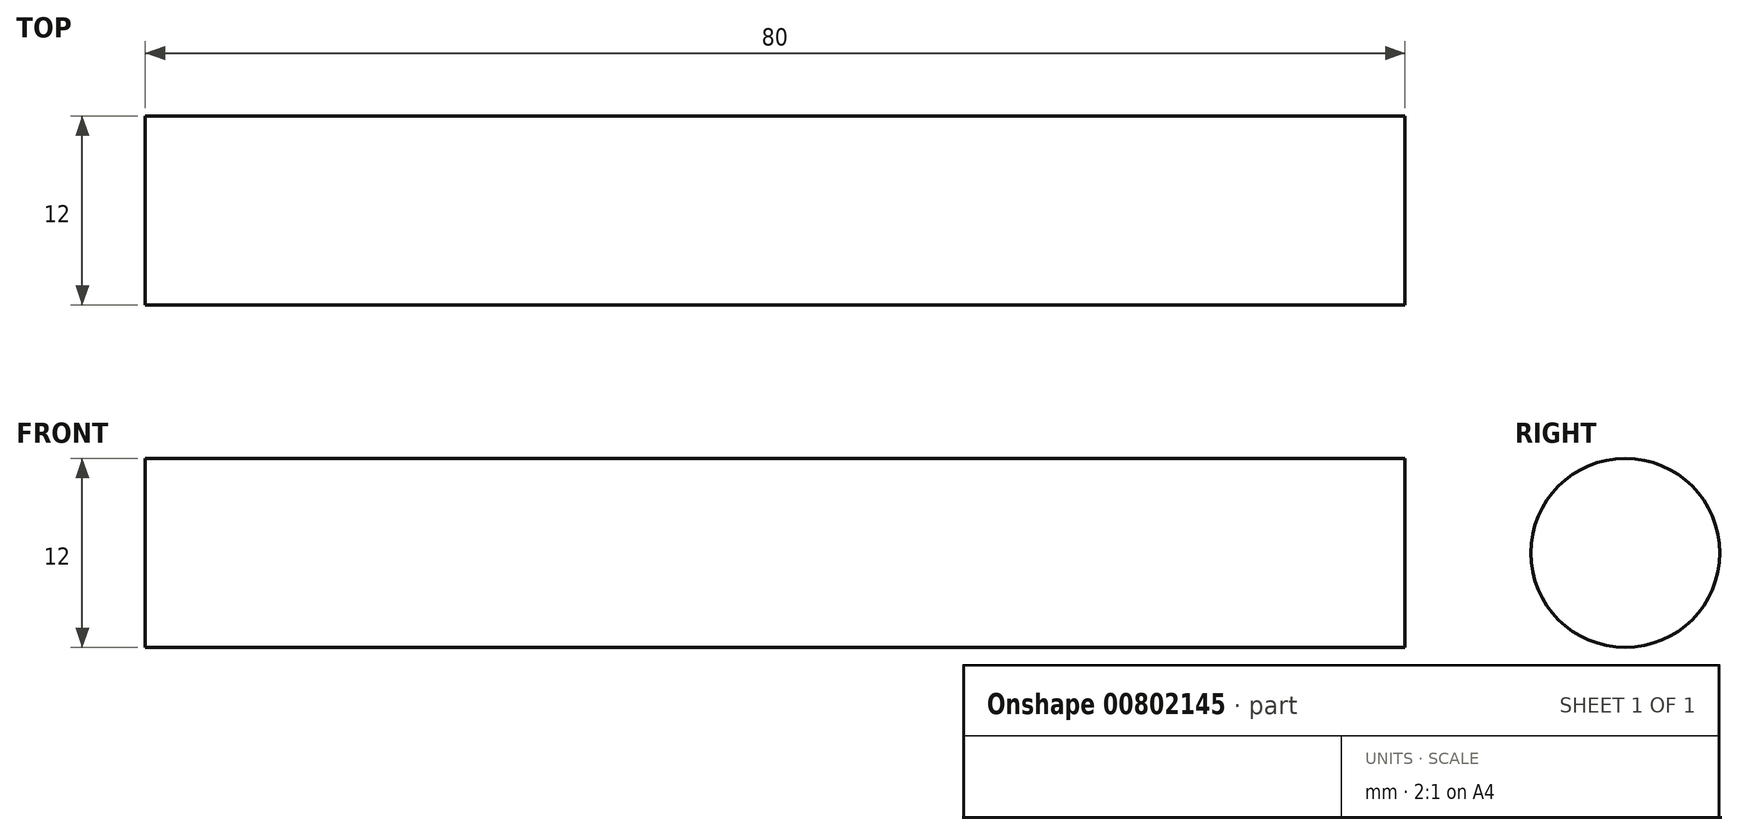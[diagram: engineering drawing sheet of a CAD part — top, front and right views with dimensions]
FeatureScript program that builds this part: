
annotation { "Feature Type Name" : "Feature", "Feature Type Description" : "" }
export const myFeature = defineFeature(function(context is Context, id is Id, definition is map)
    precondition{}
    {
        {
            var Q0;
            Q0=qCreatedBy(makeId("Right.planeOp"),FACE);
            var sketch = newSketch(context, id + "F0", { "sketchPlane" : qUnion([Q0])});
            skCircle(sketch, "E0", {"center": v(25.13, 13.04) * mm, "radius": 6 * mm});
            skSolve(sketch);
        }
        {
            var Q0;
            Q0=qSketchRegion(id+"F0",true);
            extrude(context, id + "F1", {"entities" : qUnion([Q0]), "depth" : 80 * mm, "offsetDistance" : 25 * mm});
        }
    });
